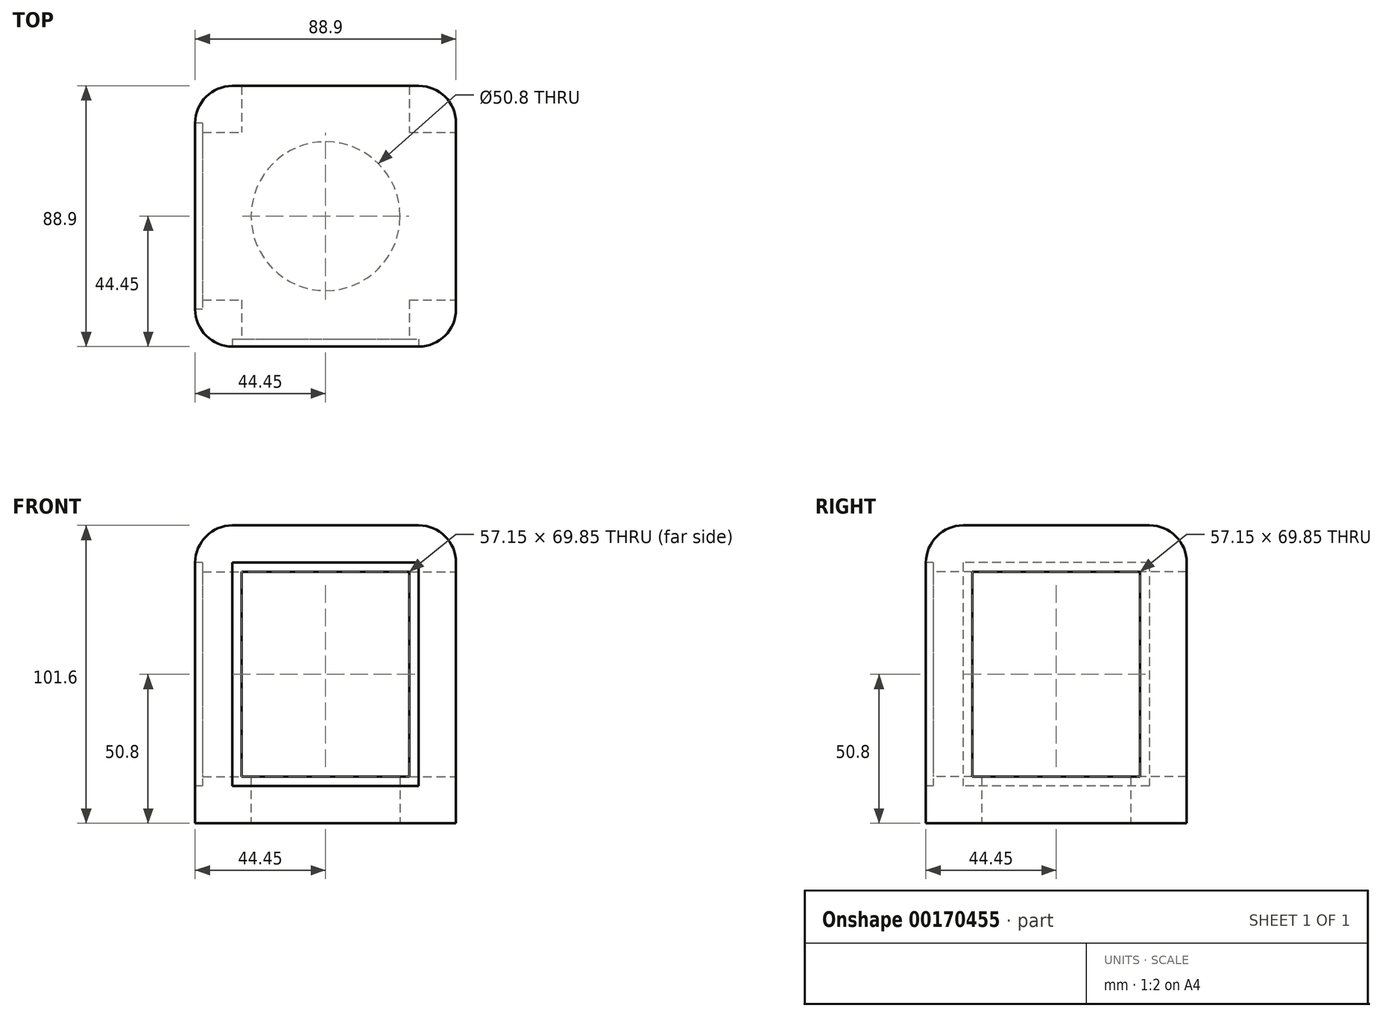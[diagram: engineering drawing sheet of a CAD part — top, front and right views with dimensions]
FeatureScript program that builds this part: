
annotation { "Feature Type Name" : "Feature", "Feature Type Description" : "" }
export const myFeature = defineFeature(function(context is Context, id is Id, definition is map)
    precondition{}
    {
        {
            var Q0;
            Q0=qCreatedBy(makeId("Top.planeOp"),FACE);
            var sketch = newSketch(context, id + "F0", { "sketchPlane" : qUnion([Q0])});
            skLineSegment(sketch, "E0.bottom", {"start": v(44.45, -44.45) * mm, "end": v(-44.45, -44.45) * mm});
            skLineSegment(sketch, "E0.top", {"start": v(44.45, 44.45) * mm, "end": v(-44.45, 44.45) * mm});
            skLineSegment(sketch, "E0.left", {"start": v(44.45, -44.45) * mm, "end": v(44.45, 44.45) * mm});
            skLineSegment(sketch, "E0.right", {"start": v(-44.45, -44.45) * mm, "end": v(-44.45, 44.45) * mm});
            skPoint(sketch, "E0.middle", {"position": v(0, 0) * mm});
            skSolve(sketch);
        }
        {
            var Q0;
            Q0=makeQuery(id+"F0.imprint","IMPRINT",FACE,{"disambiguationData":[TD([[makeQuery(id+"F0.imprint","IMPRINT",EDGE,{"derivedFrom":sQuery(id+"F0.wireOp",EDGE,"E0.bottom")}),-1.0]])]});
            extrude(context, id + "F1", {"entities" : qUnion([Q0]), "depth" : 101.6 * mm});
        }
        {
            var Q0;
            Q0=makeQuery(id+"F1.opExtrude","SWEPT_FACE",FACE,{"disambiguationData":[OSD([sQuery(id+"F0.wireOp",EDGE,"E0.bottom")])]});
            var sketch = newSketch(context, id + "F2", { "sketchPlane" : qUnion([Q0])});
            skLineSegment(sketch, "E1.bottom", {"start": v(-28.58, 85.73) * mm, "end": v(28.57, 85.73) * mm});
            skLineSegment(sketch, "E1.top", {"start": v(-28.58, 15.87) * mm, "end": v(28.58, 15.88) * mm});
            skLineSegment(sketch, "E1.left", {"start": v(-28.58, 85.73) * mm, "end": v(-28.58, 15.87) * mm});
            skLineSegment(sketch, "E1.right", {"start": v(28.58, 85.73) * mm, "end": v(28.58, 15.88) * mm});
            skSolve(sketch);
        }
        {
            var Q0;
            Q0=makeQuery(id+"F2.imprint","IMPRINT",FACE,{"disambiguationData":[TD([[makeQuery(id+"F2.imprint","IMPRINT",EDGE,{"derivedFrom":sQuery(id+"F2.wireOp",EDGE,"E1.bottom")}),-1.0]])]});
            extrude(context, id + "F3", {"entities" : qUnion([Q0]), "operationType" : NewBodyOperationType.REMOVE, "endBound" : BoundingType.THROUGH_ALL, "oppositeDirection" : true, "depth" : 25.4 * mm});
        }
        {
            var Q0;
            Q0=makeQuery(id+"F1.opExtrude","SWEPT_FACE",FACE,{"disambiguationData":[OSD([sQuery(id+"F0.wireOp",EDGE,"E0.left")])]});
            var sketch = newSketch(context, id + "F4", { "sketchPlane" : qUnion([Q0])});
            skLineSegment(sketch, "E2.bottom", {"start": v(-28.57, 15.88) * mm, "end": v(28.58, 15.88) * mm});
            skLineSegment(sketch, "E2.top", {"start": v(-28.58, 85.73) * mm, "end": v(28.58, 85.73) * mm});
            skLineSegment(sketch, "E2.left", {"start": v(-28.57, 15.88) * mm, "end": v(-28.58, 85.73) * mm});
            skLineSegment(sketch, "E2.right", {"start": v(28.58, 15.88) * mm, "end": v(28.58, 85.73) * mm});
            skSolve(sketch);
        }
        {
            var Q0;
            Q0=makeQuery(id+"F4.imprint","IMPRINT",FACE,{"disambiguationData":[TD([[makeQuery(id+"F4.imprint","IMPRINT",EDGE,{"derivedFrom":sQuery(id+"F4.wireOp",EDGE,"E2.bottom")}),1.0]])]});
            extrude(context, id + "F5", {"entities" : qUnion([Q0]), "operationType" : NewBodyOperationType.REMOVE, "endBound" : BoundingType.THROUGH_ALL, "oppositeDirection" : true, "depth" : 25.4 * mm});
        }
        {
            var Q0;
            Q0=makeQuery(id+"F1.opExtrude","CAP_FACE",FACE,{"disambiguationData":[OSD([sQuery(id+"F0.wireOp",EDGE,"E0.bottom"),sQuery(id+"F0.wireOp",EDGE,"E0.top"),sQuery(id+"F0.wireOp",EDGE,"E0.left"),sQuery(id+"F0.wireOp",EDGE,"E0.right")])],"isStart":true});
            var sketch = newSketch(context, id + "F6", { "sketchPlane" : qUnion([Q0])});
            skCircle(sketch, "E3", {"center": v(0, 0) * mm, "radius": 25.4 * mm});
            skSolve(sketch);
        }
        {
            var Q0;
            Q0=makeQuery(id+"F6.imprint","IMPRINT",FACE,{"disambiguationData":[TD([[makeQuery(id+"F6.imprint","IMPRINT",EDGE,{"derivedFrom":sQuery(id+"F6.wireOp",EDGE,"E3")}),1.0]])]});
            extrude(context, id + "F7", {"entities" : qUnion([Q0]), "operationType" : NewBodyOperationType.REMOVE, "oppositeDirection" : true, "depth" : 25.4 * mm});
        }
        {
            var Q0;
            Q0=makeQuery(id+"F1.opExtrude","SWEPT_FACE",FACE,{"disambiguationData":[OSD([sQuery(id+"F0.wireOp",EDGE,"E0.right")])]});
            var sketch = newSketch(context, id + "F8", { "sketchPlane" : qUnion([Q0])});
            skLineSegment(sketch, "E4.0", {"start": v(-31.75, 88.9) * mm, "end": v(31.75, 88.9) * mm});
            skLineSegment(sketch, "E4.1", {"start": v(-31.75, 88.9) * mm, "end": v(-31.75, 12.7) * mm});
            skLineSegment(sketch, "E4.2", {"start": v(-31.75, 12.7) * mm, "end": v(31.75, 12.7) * mm});
            skLineSegment(sketch, "E4.3", {"start": v(31.75, 88.9) * mm, "end": v(31.75, 12.7) * mm});
            skSolve(sketch);
        }
        {
            var Q0;
            Q0=makeQuery(id+"F8.imprint","IMPRINT",FACE,{"disambiguationData":[TD([[makeQuery(id+"F8.imprint","IMPRINT",EDGE,{"derivedFrom":sQuery(id+"F8.wireOp",EDGE,"E4.0")}),-1.0]])]});
            extrude(context, id + "F9", {"entities" : qUnion([Q0]), "operationType" : NewBodyOperationType.REMOVE, "oppositeDirection" : true, "depth" : 2.54 * mm});
        }
        {
            var Q0;
            Q0=makeQuery(id+"F1.opExtrude","SWEPT_FACE",FACE,{"disambiguationData":[OSD([sQuery(id+"F0.wireOp",EDGE,"E0.bottom")])]});
            var sketch = newSketch(context, id + "F10", { "sketchPlane" : qUnion([Q0])});
            skLineSegment(sketch, "E5.0", {"start": v(-31.75, 88.9) * mm, "end": v(31.75, 88.9) * mm});
            skLineSegment(sketch, "E5.1", {"start": v(-31.75, 88.9) * mm, "end": v(-31.75, 12.7) * mm});
            skLineSegment(sketch, "E5.2", {"start": v(-31.75, 12.7) * mm, "end": v(31.75, 12.7) * mm});
            skLineSegment(sketch, "E5.3", {"start": v(31.75, 88.9) * mm, "end": v(31.75, 12.7) * mm});
            skSolve(sketch);
        }
        {
            var Q0;
            Q0=makeQuery(id+"F10.imprint","IMPRINT",FACE,{"disambiguationData":[TD([[makeQuery(id+"F10.imprint","IMPRINT",EDGE,{"derivedFrom":sQuery(id+"F10.wireOp",EDGE,"E5.0")}),-1.0]])]});
            extrude(context, id + "F11", {"entities" : qUnion([Q0]), "operationType" : NewBodyOperationType.REMOVE, "oppositeDirection" : true, "depth" : 2.54 * mm});
        }
        {
            var Q0;
            Q0=makeQuery(id+"F1.opExtrude","CAP_FACE",FACE,{"disambiguationData":[OSD([sQuery(id+"F0.wireOp",EDGE,"E0.bottom"),sQuery(id+"F0.wireOp",EDGE,"E0.top"),sQuery(id+"F0.wireOp",EDGE,"E0.left"),sQuery(id+"F0.wireOp",EDGE,"E0.right")])],"isStart":false});
            var Q1;
            Q1=makeQuery(id+"F1.opExtrude","SWEPT_EDGE",EDGE,{"disambiguationData":[OSD([sQuery(id+"F0.wireOp",EDGE,"E0.bottom"),sQuery(id+"F0.wireOp",EDGE,"E0.right")])]});
            var Q2;
            Q2=makeQuery(id+"F1.opExtrude","SWEPT_EDGE",EDGE,{"disambiguationData":[OSD([sQuery(id+"F0.wireOp",EDGE,"E0.top"),sQuery(id+"F0.wireOp",EDGE,"E0.right")])]});
            var Q3;
            Q3=makeQuery(id+"F1.opExtrude","SWEPT_EDGE",EDGE,{"disambiguationData":[OSD([sQuery(id+"F0.wireOp",EDGE,"E0.top"),sQuery(id+"F0.wireOp",EDGE,"E0.left")])]});
            var Q4;
            Q4=makeQuery(id+"F1.opExtrude","SWEPT_EDGE",EDGE,{"disambiguationData":[OSD([sQuery(id+"F0.wireOp",EDGE,"E0.bottom"),sQuery(id+"F0.wireOp",EDGE,"E0.left")])]});
            fillet(context, id + "F12", {"entities" : qUnion([Q0, Q1, Q2, Q3, Q4]), "radius" : 12.7 * mm, "tangentPropagation" : true, "allowEdgeOverflow" : false});
        }
    });
